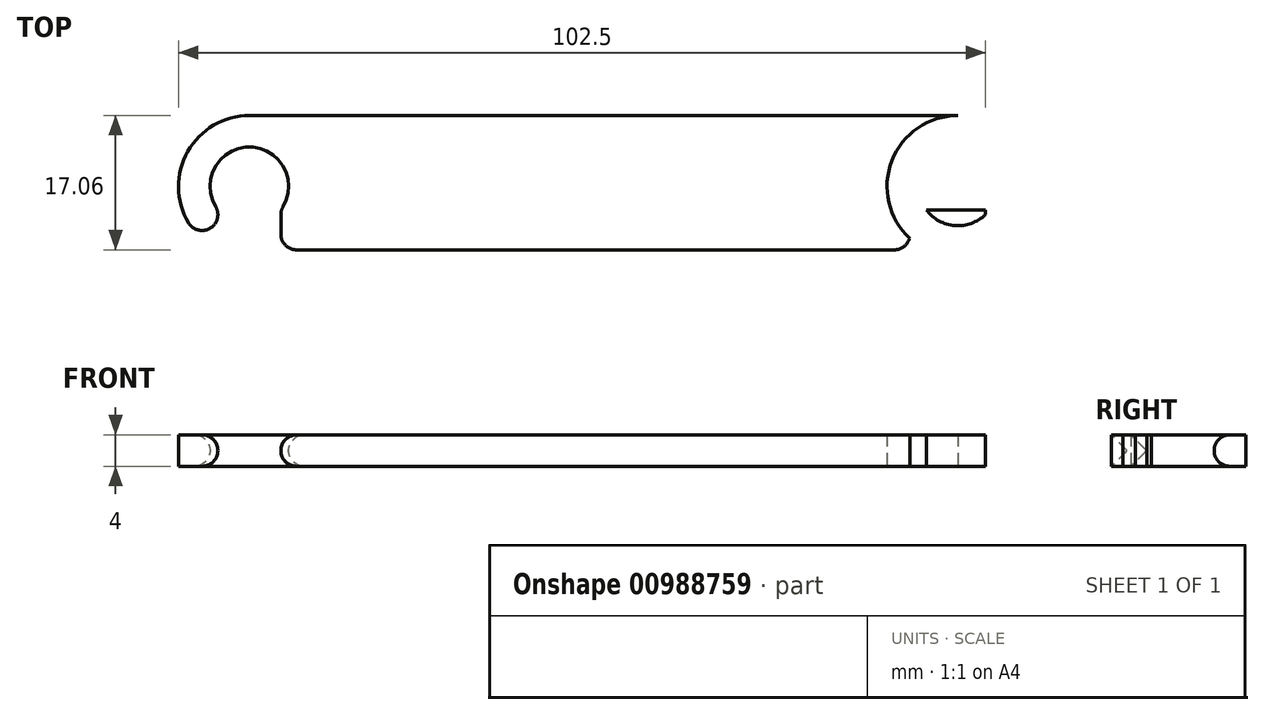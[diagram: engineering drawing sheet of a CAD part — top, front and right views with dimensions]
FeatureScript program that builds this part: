
annotation { "Feature Type Name" : "Feature", "Feature Type Description" : "" }
export const myFeature = defineFeature(function(context is Context, id is Id, definition is map)
    precondition{}
    {
        {
            var Q0;
            Q0=qCreatedBy(makeId("Top.planeOp"),FACE);
            var Q1;
            Q1=qCreatedBy(makeId("Top.planeOp"),FACE);
            var sketch = newSketch(context, id + "F0", { "sketchPlane" : qUnion([Q0, Q1])});
            skCircle(sketch, "E0", {"center": v(-45, 0) * mm, "radius": 5 * mm});
            skCircle(sketch, "E1", {"center": v(-45, 0) * mm, "radius": 9 * mm});
            skLineSegment(sketch, "E2", {"start": v(0, 16.8) * mm, "end": v(0, -13.62) * mm, "construction": true});
            skCircle(sketch, "E3.MirrorC", {"center": v(45, 0) * mm, "radius": 5 * mm});
            skCircle(sketch, "E4.MirrorC", {"center": v(45, 0) * mm, "radius": 9 * mm});
            skLineSegment(sketch, "E5", {"start": v(-45, 9) * mm, "end": v(45, 9) * mm});
            skLineSegment(sketch, "E6.top", {"start": v(-46.22, 0) * mm, "end": v(-53.72, 0) * mm});
            skPoint(sketch, "E7", {"position": v(41, -8.06) * mm});
            skLineSegment(sketch, "E8.MirrorCS", {"start": v(-41, -8.06) * mm, "end": v(-41, 0) * mm});
            skLineSegment(sketch, "E9.MirrorCS", {"start": v(-49, 0) * mm, "end": v(-41, 0) * mm});
            skLineSegment(sketch, "E10.MirrorCS", {"start": v(-49, -8.06) * mm, "end": v(-49, 0) * mm});
            skLineSegment(sketch, "E11.MirrorCS", {"start": v(-49, -8.06) * mm, "end": v(-41, -8.06) * mm});
            skPoint(sketch, "E12.MirrorP", {"position": v(-41, -8.06) * mm});
            skPoint(sketch, "E13", {"position": v(48.5, -13.14) * mm});
            skPoint(sketch, "E14.MirrorP", {"position": v(-48.5, -13.14) * mm});
            skLineSegment(sketch, "E15.MirrorCS", {"start": v(-48.5, -13.14) * mm, "end": v(-41, -8.06) * mm});
            skLineSegment(sketch, "E16.MirrorCS", {"start": v(-48.5, -13.14) * mm, "end": v(-49.11, -8.06) * mm});
            skPoint(sketch, "E17", {"position": v(38.9, -6.62) * mm});
            skPoint(sketch, "E18", {"position": v(41, -3) * mm});
            skLineSegment(sketch, "E19", {"start": v(41, -3) * mm, "end": v(38.9, -6.62) * mm});
            skLineSegment(sketch, "E20", {"start": v(35.3, -13.14) * mm, "end": v(38.9, -6.62) * mm});
            skLineSegment(sketch, "E21", {"start": v(35.3, -13.14) * mm, "end": v(48.5, -13.14) * mm});
            skLineSegment(sketch, "E22", {"start": v(48.5, -3) * mm, "end": v(48.5, -13.14) * mm});
            skLineSegment(sketch, "E23", {"start": v(48.5, -3) * mm, "end": v(41, -3) * mm});
            skLineSegment(sketch, "E24", {"start": v(-41, -8.06) * mm, "end": v(41, -8.06) * mm});
            skSolve(sketch);
        }
        {
            var Q0;
            {var subQ5=sQuery(id+"F0.wireOp",EDGE,"E5");Q0=makeQuery(id+"F0.imprint","IMPRINT",FACE,{"disambiguationData":[TD([[makeQuery(id+"F0.imprint","IMPRINT",EDGE,{"derivedFrom":subQ5}),-1.0]])]});}
            var Q1;
            {var subQ0=sQuery(id+"F0.wireOp",EDGE,"E6.left");var subQ1=sQuery(id+"F0.wireOp",EDGE,"E0");var subQ2=makeQuery(id+"F0.imprint","INTERSECT",VERTEX,{"derivedFrom":[subQ1,subQ0]});Q1=makeQuery(id+"F0.imprint","IMPRINT",FACE,{"disambiguationData":[TD([[makeQuery(id+"F0.imprint","IMPRINT",EDGE,{"disambiguationData":[TD([[subQ2,-1.0]])],"derivedFrom":subQ1}),-1.0]])]});}
            var Q2;
            {var subQ0=sQuery(id+"F0.wireOp",EDGE,"Mlm7viBo-fhNu-2G3E-vQz7-4U8KD43A8j40.left");var subQ3=sQuery(id+"F0.wireOp",EDGE,"E3.MirrorC");var subQ4=makeQuery(id+"F0.imprint","INTERSECT",VERTEX,{"derivedFrom":[subQ3,subQ0]});Q2=makeQuery(id+"F0.imprint","IMPRINT",FACE,{"disambiguationData":[TD([[makeQuery(id+"F0.imprint","IMPRINT",EDGE,{"disambiguationData":[TD([[subQ4,1.0]])],"derivedFrom":subQ3}),1.0]])]});}
            extrude(context, id + "F1", {"entities" : qUnion([Q0, Q1, Q2]), "depth" : 4 * mm, "offsetDistance" : 25 * mm});
        }
        {
            var Q0;
            Q0=makeQuery(id+"F1.opExtrude","SWEPT_FACE",FACE,{"disambiguationData":[OSD([sQuery(id+"F0.wireOp",EDGE,"E3.MirrorC")])]});
            var Q1;
            Q1=makeQuery(id+"F1.opExtrude","SWEPT_FACE",FACE,{"disambiguationData":[OSD([sQuery(id+"F0.wireOp",EDGE,"Mlm7viBo-fhNu-2G3E-vQz7-4U8KD43A8j40.right")])]});
            var Q2;
            Q2=makeQuery(id+"F1.opExtrude","SWEPT_FACE",FACE,{"disambiguationData":[OSD([sQuery(id+"F0.wireOp",EDGE,"Mlm7viBo-fhNu-2G3E-vQz7-4U8KD43A8j40.left")])]});
            var Q3;
            Q3=makeQuery(id+"F1.opExtrude","SWEPT_FACE",FACE,{"disambiguationData":[OSD([sQuery(id+"F0.wireOp",EDGE,"E6.left")])]});
            var Q4;
            Q4=makeQuery(id+"F1.opExtrude","SWEPT_FACE",FACE,{"disambiguationData":[OSD([sQuery(id+"F0.wireOp",EDGE,"E0")])]});
            var Q5;
            Q5=makeQuery(id+"F1.opExtrude","SWEPT_FACE",FACE,{"disambiguationData":[OSD([sQuery(id+"F0.wireOp",EDGE,"E6.right")])]});
            fillet(context, id + "F2", {"entities" : qUnion([Q0, Q1, Q2, Q3, Q4, Q5]), "radius" : 2 * mm, "allowEdgeOverflow" : false});
        }
        {
            var Q0;
            Q0=makeQuery(id+"F1.opExtrude","SWEPT_EDGE",EDGE,{"disambiguationData":[OSD([sQuery(id+"F0.wireOp",EDGE,"E1"),sQuery(id+"F0.wireOp",EDGE,"E10.MirrorCS"),sQuery(id+"F0.wireOp",EDGE,"E11.MirrorCS"),sQuery(id+"F0.wireOp",EDGE,"E16.MirrorCS")])]});
            var Q1;
            {var subQ0=sQuery(id+"F0.wireOp",EDGE,"E10.MirrorCS");Q1=makeQuery(id+"F2.opFillet","BLEND_EDGE",EDGE,{"blendedFrom":[makeQuery(id+"F1.opExtrude","SWEPT_EDGE",EDGE,{"disambiguationData":[OSD([sQuery(id+"F0.wireOp",EDGE,"E0"),subQ0])]}),makeQuery(id+"F1.opExtrude","SWEPT_FACE",FACE,{"disambiguationData":[OSD([subQ0])]})],"blendedInto":[makeQuery(id+"F1.opExtrude","SWEPT_FACE",FACE,{"disambiguationData":[OSD([subQ0])]})]});}
            var Q2;
            Q2=makeQuery(id+"F1.opExtrude","SWEPT_EDGE",EDGE,{"disambiguationData":[OSD([sQuery(id+"F0.wireOp",EDGE,"E1"),sQuery(id+"F0.wireOp",EDGE,"E8.MirrorCS"),sQuery(id+"F0.wireOp",EDGE,"E11.MirrorCS"),sQuery(id+"F0.wireOp",EDGE,"2IUsfnSs-gInB-SSYq-R6zO-fKnSITSIE1mo"),sQuery(id+"F0.wireOp",EDGE,"E15.MirrorCS")])]});
            var Q3;
            {var subQ0=sQuery(id+"F0.wireOp",EDGE,"E8.MirrorCS");Q3=makeQuery(id+"F2.opFillet","BLEND_EDGE",EDGE,{"blendedFrom":[makeQuery(id+"F1.opExtrude","SWEPT_EDGE",EDGE,{"disambiguationData":[OSD([sQuery(id+"F0.wireOp",EDGE,"E0"),subQ0])]}),makeQuery(id+"F1.opExtrude","SWEPT_FACE",FACE,{"disambiguationData":[OSD([subQ0])]})],"blendedInto":[makeQuery(id+"F1.opExtrude","SWEPT_FACE",FACE,{"disambiguationData":[OSD([subQ0])]})]});}
            var Q4;
            Q4=makeQuery(id+"F1.opExtrude","CAP_EDGE",EDGE,{"disambiguationData":[OSD([sQuery(id+"F0.wireOp",EDGE,"E8.MirrorCS")])],"isStart":false});
            var Q5;
            Q5=makeQuery(id+"F1.opExtrude","CAP_EDGE",EDGE,{"disambiguationData":[OSD([sQuery(id+"F0.wireOp",EDGE,"E8.MirrorCS")])],"isStart":true});
            var Q6;
            Q6=makeQuery(id+"F1.opExtrude","SWEPT_FACE",FACE,{"disambiguationData":[OSD([sQuery(id+"F0.wireOp",EDGE,"E10.MirrorCS")])]});
            fillet(context, id + "F3", {"entities" : qUnion([Q0, Q1, Q2, Q3, Q4, Q5, Q6]), "radius" : 2 * mm, "tangentPropagation" : true, "allowEdgeOverflow" : false});
        }
        {
            var Q0;
            Q0=makeQuery(id+"F1.opExtrude","SWEPT_FACE",FACE,{"disambiguationData":[OSD([sQuery(id+"F0.wireOp",EDGE,"E19")])]});
            var Q1;
            Q1=makeQuery(id+"F1.opExtrude","SWEPT_FACE",FACE,{"disambiguationData":[OSD([sQuery(id+"F0.wireOp",EDGE,"E22")])]});
            var Q2;
            Q2=makeQuery(id+"F1.opExtrude","SWEPT_EDGE",EDGE,{"disambiguationData":[OSD([sQuery(id+"F0.wireOp",EDGE,"E20"),sQuery(id+"F0.wireOp",EDGE,"E24")])]});
            fillet(context, id + "F4", {"entities" : qUnion([Q0, Q1, Q2]), "radius" : 2 * mm, "tangentPropagation" : true, "allowEdgeOverflow" : false});
        }
    });
